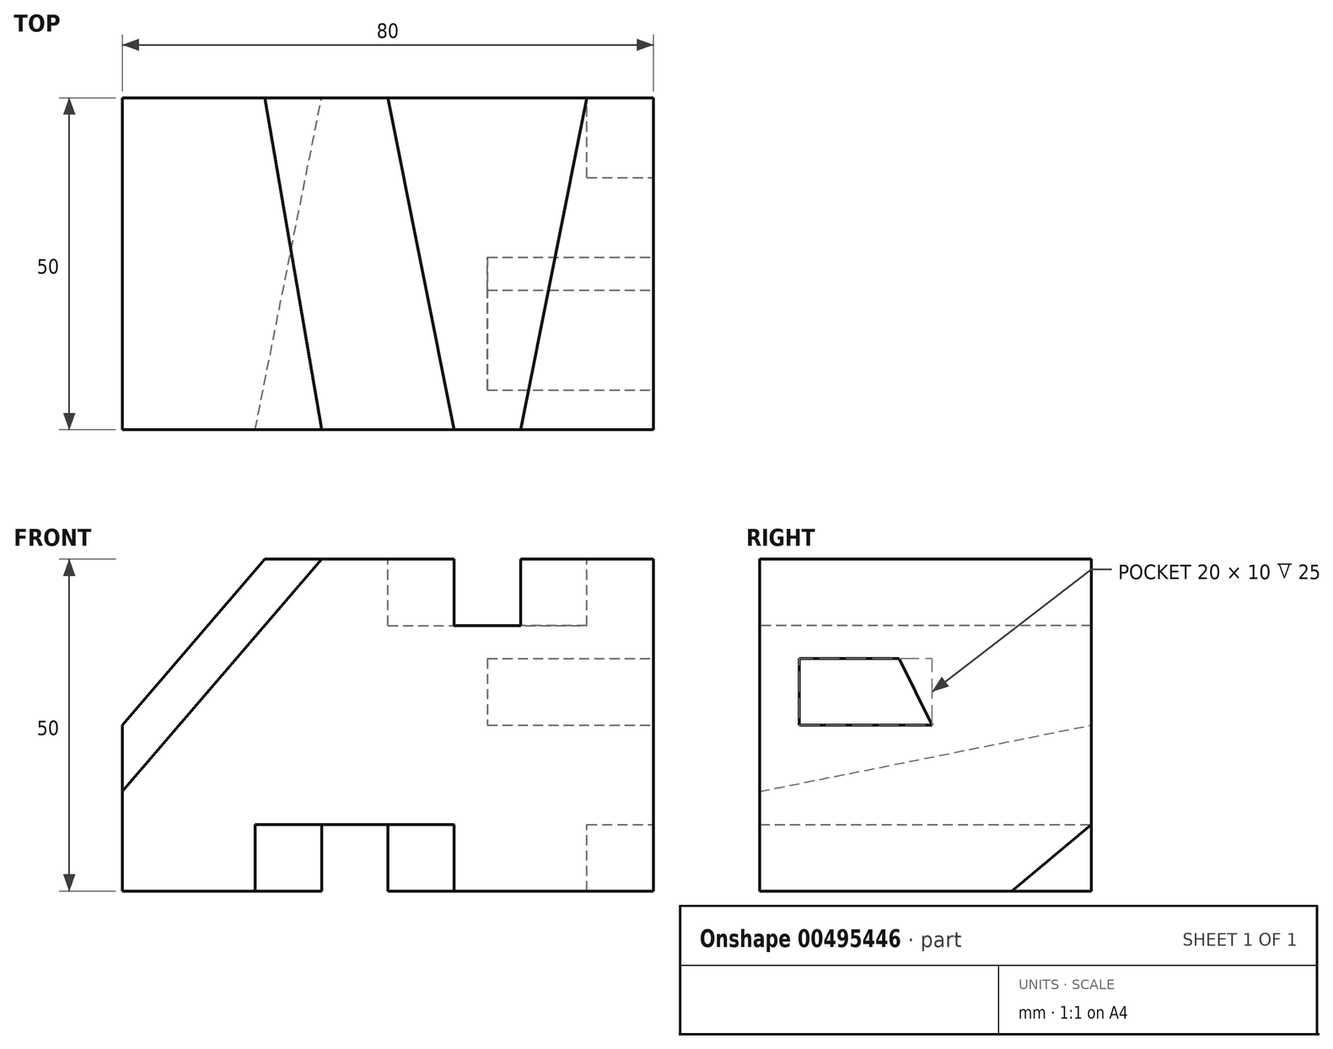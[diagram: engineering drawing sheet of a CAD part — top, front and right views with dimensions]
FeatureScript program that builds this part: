
annotation { "Feature Type Name" : "Feature", "Feature Type Description" : "" }
export const myFeature = defineFeature(function(context is Context, id is Id, definition is map)
    precondition{}
    {
        {
            var Q0;
            Q0=qCreatedBy(makeId("Front.planeOp"),FACE);
            var sketch = newSketch(context, id + "F0", { "sketchPlane" : qUnion([Q0])});
            skLineSegment(sketch, "E0.bottom", {"start": v(0, 0) * mm, "end": v(80, 0) * mm});
            skLineSegment(sketch, "E0.top", {"start": v(0, 50) * mm, "end": v(80, 50) * mm});
            skLineSegment(sketch, "E0.left", {"start": v(0, 0) * mm, "end": v(0, 50) * mm});
            skLineSegment(sketch, "E0.right", {"start": v(80, 0) * mm, "end": v(80, 50) * mm});
            skSolve(sketch);
        }
        {
            var Q0;
            Q0=makeQuery(id+"F0.imprint","IMPRINT",FACE,{"disambiguationData":[TD([[makeQuery(id+"F0.imprint","IMPRINT",EDGE,{"derivedFrom":sQuery(id+"F0.wireOp",EDGE,"E0.bottom")}),1.0]])]});
            extrude(context, id + "F1", {"entities" : qUnion([Q0]), "depth" : 50 * mm});
        }
        {
            var Q0;
            Q0=makeQuery(id+"F1.opExtrude","SWEPT_FACE",FACE,{"disambiguationData":[OSD([sQuery(id+"F0.wireOp",EDGE,"E0.top")])]});
            var sketch = newSketch(context, id + "F2", { "sketchPlane" : qUnion([Q0])});
            skLineSegment(sketch, "E1", {"start": v(0, 0) * mm, "end": v(20, 0) * mm});
            skLineSegment(sketch, "E2", {"start": v(20, 0) * mm, "end": v(30, -50) * mm});
            skLineSegment(sketch, "E3", {"start": v(30, -50) * mm, "end": v(0, -50) * mm});
            skLineSegment(sketch, "E4", {"start": v(0, -50) * mm, "end": v(0, 0) * mm});
            skLineSegment(sketch, "E5", {"start": v(30, -50) * mm, "end": v(50, -50) * mm});
            skLineSegment(sketch, "E6", {"start": v(50, -50) * mm, "end": v(60, -50) * mm});
            skLineSegment(sketch, "E7", {"start": v(0, 0) * mm, "end": v(40, 0) * mm});
            skLineSegment(sketch, "E8", {"start": v(80, 0) * mm, "end": v(70, 0) * mm});
            skLineSegment(sketch, "E9", {"start": v(40, 0) * mm, "end": v(50, -50) * mm});
            skLineSegment(sketch, "E10", {"start": v(70, 0) * mm, "end": v(60, -50) * mm});
            skLineSegment(sketch, "E11", {"start": v(40, 0) * mm, "end": v(70, 0) * mm});
            skSolve(sketch);
        }
        {
            var Q0;
            Q0=makeQuery(id+"F1.opExtrude","SWEPT_FACE",FACE,{"disambiguationData":[OSD([sQuery(id+"F0.wireOp",EDGE,"E0.left")])]});
            var sketch = newSketch(context, id + "F3", { "sketchPlane" : qUnion([Q0])});
            skLineSegment(sketch, "E12", {"start": v(50, 0) * mm, "end": v(50, 15) * mm});
            skLineSegment(sketch, "E13", {"start": v(50, 15) * mm, "end": v(0, 25) * mm});
            skLineSegment(sketch, "E14", {"start": v(0, 25) * mm, "end": v(0, 0) * mm});
            skLineSegment(sketch, "E15", {"start": v(0, 0) * mm, "end": v(50, 0) * mm});
            skSolve(sketch);
        }
        {
            var Q0;
            Q0=makeQuery(id+"F2.imprint","IMPRINT",FACE,{"disambiguationData":[TD([[makeQuery(id+"F2.imprint","IMPRINT",EDGE,{"derivedFrom":sQuery(id+"F2.wireOp",EDGE,"E6")}),1.0]])]});
            extrude(context, id + "F4", {"entities" : qUnion([Q0]), "operationType" : NewBodyOperationType.REMOVE, "oppositeDirection" : true, "depth" : 10 * mm});
        }
        {
            var Q0;
            Q0=makeQuery(id+"F1.opExtrude","SWEPT_FACE",FACE,{"disambiguationData":[OSD([sQuery(id+"F0.wireOp",EDGE,"E0.right")])]});
            var sketch = newSketch(context, id + "F5", { "sketchPlane" : qUnion([Q0])});
            skLineSegment(sketch, "E16", {"start": v(-50, 0) * mm, "end": v(-44, 0) * mm});
            skLineSegment(sketch, "E17", {"start": v(-44, 0) * mm, "end": v(-44, 25) * mm});
            skLineSegment(sketch, "E18", {"start": v(-44, 25) * mm, "end": v(-44, 35) * mm});
            skLineSegment(sketch, "E19", {"start": v(-44, 35) * mm, "end": v(-29, 35) * mm});
            skLineSegment(sketch, "E20", {"start": v(-29, 35) * mm, "end": v(-24, 25) * mm});
            skLineSegment(sketch, "E21", {"start": v(-24, 25) * mm, "end": v(-44, 25) * mm});
            skLineSegment(sketch, "E22", {"start": v(-29, 35) * mm, "end": v(-29, 25) * mm});
            skLineSegment(sketch, "E23", {"start": v(-29, 25) * mm, "end": v(-24, 25) * mm});
            skLineSegment(sketch, "E24", {"start": v(0, 0) * mm, "end": v(0, 10) * mm});
            skLineSegment(sketch, "E25", {"start": v(0, 10) * mm, "end": v(-12, 0) * mm});
            skLineSegment(sketch, "E26", {"start": v(-12, 0) * mm, "end": v(0, 0) * mm});
            skSolve(sketch);
        }
        {
            var Q0;
            Q0=makeQuery(id+"F5.imprint","IMPRINT",FACE,{"disambiguationData":[TD([[makeQuery(id+"F5.imprint","IMPRINT",EDGE,{"derivedFrom":sQuery(id+"F5.wireOp",EDGE,"E18")}),-1.0]])]});
            var Q1;
            Q1=makeQuery(id+"F5.imprint","IMPRINT",FACE,{"disambiguationData":[TD([[makeQuery(id+"F5.imprint","IMPRINT",EDGE,{"derivedFrom":sQuery(id+"F5.wireOp",EDGE,"E20")}),-1.0]])]});
            extrude(context, id + "F6", {"entities" : qUnion([Q0, Q1]), "operationType" : NewBodyOperationType.REMOVE, "oppositeDirection" : true, "depth" : 25 * mm, "offsetDistance" : 25 * mm});
        }
        {
            var Q0;
            Q0=makeQuery(id+"F5.imprint","IMPRINT",FACE,{"disambiguationData":[TD([[makeQuery(id+"F5.imprint","IMPRINT",EDGE,{"derivedFrom":sQuery(id+"F5.wireOp",EDGE,"E24")}),1.0]])]});
            extrude(context, id + "F7", {"entities" : qUnion([Q0]), "operationType" : NewBodyOperationType.REMOVE, "oppositeDirection" : true, "depth" : 10 * mm, "offsetDistance" : 25 * mm});
        }
        {
            var Q0;
            Q0=makeQuery(id+"F1.opExtrude","SWEPT_FACE",FACE,{"disambiguationData":[OSD([sQuery(id+"F0.wireOp",EDGE,"E0.bottom")])]});
            var sketch = newSketch(context, id + "F8", { "sketchPlane" : qUnion([Q0])});
            skLineSegment(sketch, "E27", {"start": v(0, 0) * mm, "end": v(30, 0) * mm});
            skLineSegment(sketch, "E28", {"start": v(0, 50) * mm, "end": v(20, 50) * mm});
            skLineSegment(sketch, "E29", {"start": v(20, 50) * mm, "end": v(30, 0) * mm});
            skLineSegment(sketch, "E30", {"start": v(30, 0) * mm, "end": v(40, 0) * mm});
            skLineSegment(sketch, "E31", {"start": v(20, 50) * mm, "end": v(50, 50) * mm});
            skLineSegment(sketch, "E32", {"start": v(50, 50) * mm, "end": v(40, 0) * mm});
            skSolve(sketch);
        }
        {
            var Q0;
            Q0=makeQuery(id+"F8.imprint","IMPRINT",FACE,{"disambiguationData":[TD([[makeQuery(id+"F8.imprint","IMPRINT",EDGE,{"derivedFrom":sQuery(id+"F8.wireOp",EDGE,"E29")}),1.0]])]});
            extrude(context, id + "F9", {"entities" : qUnion([Q0]), "operationType" : NewBodyOperationType.REMOVE, "oppositeDirection" : true, "depth" : 10 * mm, "offsetDistance" : 25 * mm});
        }
        {
            var Q0;
            {var subQ1=sQuery(id+"F0.wireOp",EDGE,"E0.left");var subQ2=sQuery(id+"F0.wireOp",EDGE,"E0.top");Q0=makeQuery(id+"F4.boolean.opBoolean","SPLIT",FACE,{"disambiguationData":[TD([makeQuery(id+"F1.opExtrude","SWEPT_FACE",FACE,{"disambiguationData":[OSD([subQ1])]})])],"derivedFrom":makeQuery(id+"F1.opExtrude","SWEPT_FACE",FACE,{"disambiguationData":[OSD([subQ2])]})});}
            var sketch = newSketch(context, id + "F10", { "sketchPlane" : qUnion([Q0])});
            skLineSegment(sketch, "E33", {"start": v(0, 0) * mm, "end": v(20, 0) * mm});
            skLineSegment(sketch, "E34", {"start": v(20, 0) * mm, "end": v(30, -50) * mm});
            skLineSegment(sketch, "E35", {"start": v(30, -50) * mm, "end": v(0, -50) * mm});
            skSolve(sketch);
        }
        {
            var Q0;
            Q0=makeQuery(id+"F1.opExtrude","CAP_FACE",FACE,{"disambiguationData":[OSD([sQuery(id+"F0.wireOp",EDGE,"E0.bottom"),sQuery(id+"F0.wireOp",EDGE,"E0.top"),sQuery(id+"F0.wireOp",EDGE,"E0.left"),sQuery(id+"F0.wireOp",EDGE,"E0.right")])],"isStart":false});
            var sketch = newSketch(context, id + "F11", { "sketchPlane" : qUnion([Q0])});
            skLineSegment(sketch, "E36", {"start": v(30, 50) * mm, "end": v(0, 15) * mm});
            skSolve(sketch);
        }
        {
            var Q0;
            {var subQ0=sQuery(id+"F11.wireOp",EDGE,"E36");Q0=makeQuery(id+"F11.imprint","IMPRINT",FACE,{"disambiguationData":[TD([[makeQuery(id+"F11.imprint","IMPRINT",EDGE,{"derivedFrom":subQ0}),-1.0]])]});}
            var Q1;
            Q1=sQuery(id+"F3.wireOp",EDGE,"E13");
            sweep(context, id + "F12", {"operationType" : NewBodyOperationType.REMOVE, "profiles" : qUnion([Q0]), "path" : qUnion([Q1])});
        }
    });
